# Revit family: Access_Door-Heavy_Duty-Cendrex-Large_Openings-Drywall_Flange-(LHD-GYP)
name_source: partatom
category: Specialty Equipment
revit_build: Autodesk Revit Architecture 2013 (Build: 20130531_2115(x64)
units: mm (PartAtom-declared; Revit-internal decimal feet)

## types (2) — shared parameters
Assembly Code = C1020700
Available Options = http://cendrex.com
Cendrex LEED Ready Program = http://www.cendrex.com
Construction Material = Metal - Cendrex - Aluminum
Default Elevation = 0"
Description = Heavy duty access door for large openings
Door Height = 48"
Door Height Calc = 48"
Door Width = 48"
Door Width Calc = 48"
Finish = Metal - Cendrex - Powder Coated White
Frame Depth = 2"
Height Actual = 50"
Manufacturer = Cendrex
Model = LHD-GYP
Product Documentation Link = http://cendrex.com
Product Page URL = http://cendrex.com
URL = http://www.cendrex.com
Width Actual = 50"

## type names (no varying parameters)
- 48 x 48
- Custom

## geometry (parser evidence)
native form markers: Blend x5, Sweep x14
no freeform markers — native parametric forms only
